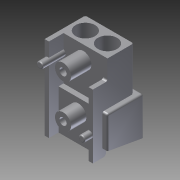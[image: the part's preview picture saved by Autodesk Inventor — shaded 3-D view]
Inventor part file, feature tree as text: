
AUTODESK INVENTOR PART (.ipt)
format: ipt  version: 2013 (Build 170138000, 138)  size: 358,912 bytes
history: native  units: mm
features: chamfer x1, imported_body x1
ambient origin geometry x8: Origin, YZ Plane, XZ Plane, XY Plane, X Axis, Y Axis, Z Axis, Center Point
feature tree (2):
  chamfer  "Chamfer1"  [1 undecoded]
  imported_body  "Base1"
note: 1 required parameter value undecoded (feature->parameter linkage not recoverable at this tier; creation-order binding heuristic only, values carry confidence <= 0.55)
